# Revit family: Pipe Support Rod Hanger with Clamp & Spring
name_source: partatom
category: Pipe Fittings
revit_build: Autodesk Revit 2014 (Build: 20130308_1515(x64)
units: mm (PartAtom-declared; Revit-internal decimal feet)

## types (14) — shared parameters
Anchor Bolt = Eye Nut : M16
Fasteners = Fasteners
Neoprene Pad = Rubber
Pipe Support = Pipe Support
Spring = Spring

## per-type parameters (varying)
| type | Anchor Nut | Eye Nut |
| 1200 | Nut : M44 | Eye Nut : M44 |
| 600 | Nut : M32 | Eye Nut : M32 |
| 300 | Nut : M22 | Eye Nut : M22 |
| 100 | Nut : M16 | Eye Nut : M16 |
| 150 | Nut : M20 | Eye Nut : M20 |
| 200 | Nut : M22 | Eye Nut : M22 |
| 250 | Nut : M22 | Eye Nut : M22 |
| 350 | Nut : M25 | Eye Nut : M24 |
| 400 | Nut : M25 | Eye Nut : M24 |
| 450 | Nut : M25 | Eye Nut : M24 |
| 500 | Nut : M32 | Eye Nut : M32 |
| 750 | Nut : M32 | Eye Nut : M32 |
| 900 | Nut : M38 | Eye Nut : M38 |
| 1050 | Nut : M38 | Eye Nut : M38 |

## geometry (parser evidence)
native form markers: Sweep x8
no freeform markers — native parametric forms only
